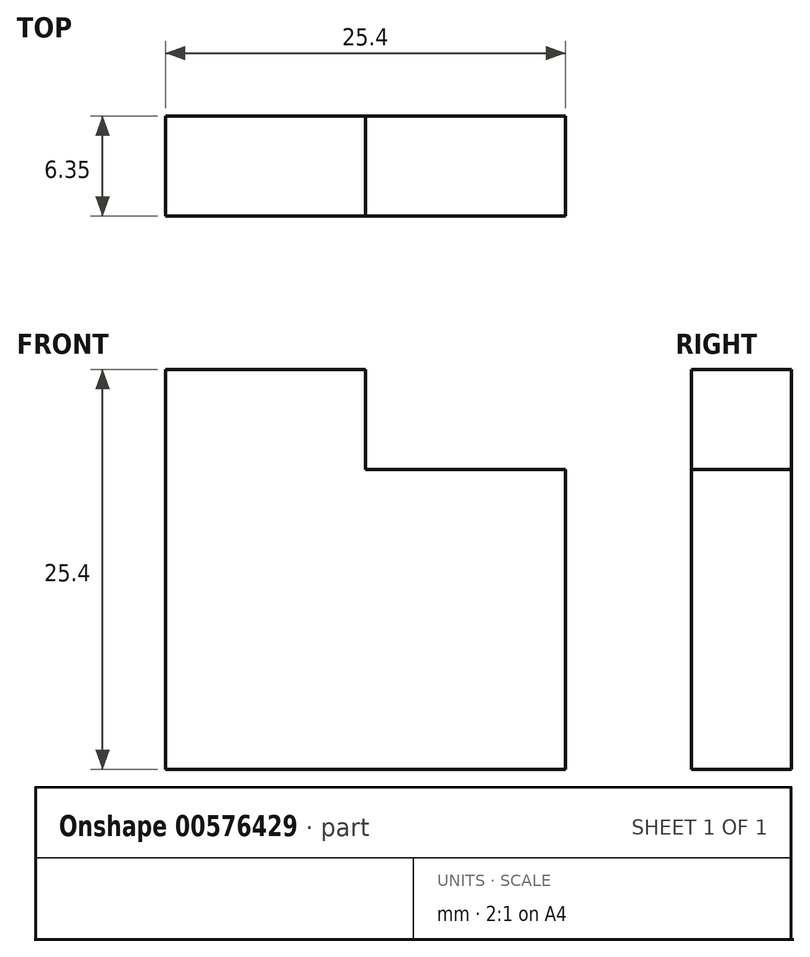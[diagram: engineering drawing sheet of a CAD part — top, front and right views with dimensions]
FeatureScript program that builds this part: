
annotation { "Feature Type Name" : "Feature", "Feature Type Description" : "" }
export const myFeature = defineFeature(function(context is Context, id is Id, definition is map)
    precondition{}
    {
        {
            var Q0;
            Q0=qCreatedBy(makeId("Front.planeOp"),FACE);
            var sketch = newSketch(context, id + "F0", { "sketchPlane" : qUnion([Q0])});
            skLineSegment(sketch, "E0", {"start": v(-37.57, 0) * mm, "end": v(-37.57, -25.4) * mm});
            skLineSegment(sketch, "E1", {"start": v(-37.57, -25.4) * mm, "end": v(-12.17, -25.4) * mm});
            skLineSegment(sketch, "E2", {"start": v(-12.17, -25.4) * mm, "end": v(-12.17, -6.35) * mm});
            skLineSegment(sketch, "E3", {"start": v(-12.17, -6.35) * mm, "end": v(-24.87, -6.35) * mm});
            skLineSegment(sketch, "E4", {"start": v(-24.87, -6.35) * mm, "end": v(-24.87, 0) * mm});
            skLineSegment(sketch, "E5", {"start": v(-24.87, 0) * mm, "end": v(-37.57, 0) * mm});
            skLineSegment(sketch, "E6", {"start": v(-37.57, 0) * mm, "end": v(-37.57, 0) * mm});
            skSolve(sketch);
        }
        {
            var Q0;
            Q0=makeQuery(id+"F0.imprint","IMPRINT",FACE,{"disambiguationData":[TD([[makeQuery(id+"F0.imprint","IMPRINT",EDGE,{"derivedFrom":sQuery(id+"F0.wireOp",EDGE,"E0")}),1.0]])]});
            extrude(context, id + "F1", {"entities" : qUnion([Q0]), "depth" : 6.35 * mm, "offsetDistance" : 25.4 * mm});
        }
    });
